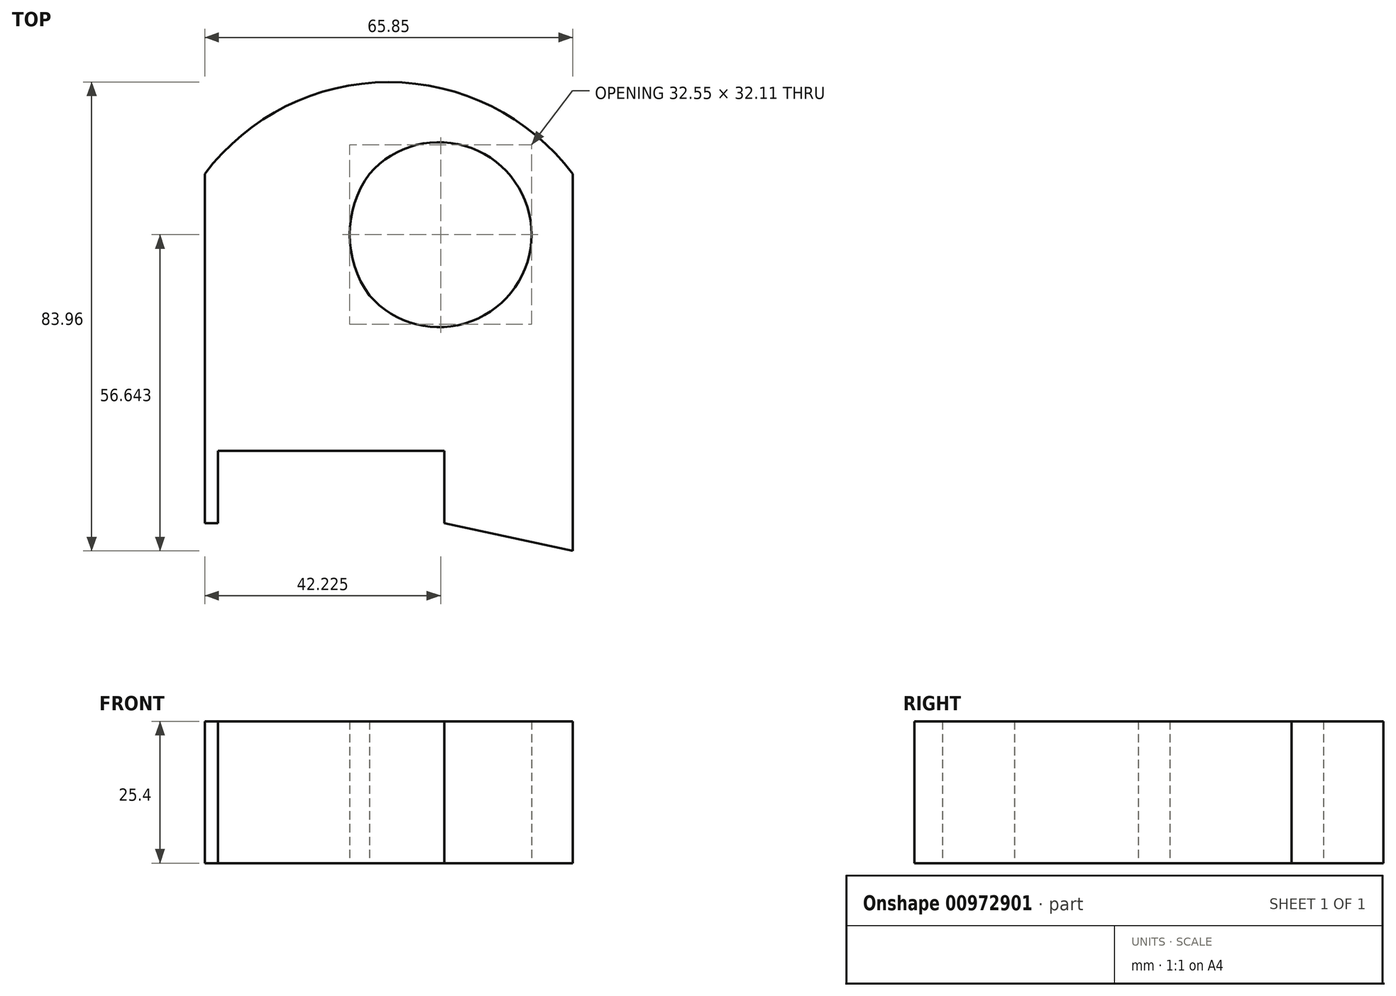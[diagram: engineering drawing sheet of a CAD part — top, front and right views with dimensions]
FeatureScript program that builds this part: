
annotation { "Feature Type Name" : "Feature", "Feature Type Description" : "" }
export const myFeature = defineFeature(function(context is Context, id is Id, definition is map)
    precondition{}
    {
        {
            var Q0;
            Q0=qCreatedBy(makeId("Top.planeOp"),FACE);
            var sketch = newSketch(context, id + "F0", { "sketchPlane" : qUnion([Q0])});
            skLineSegment(sketch, "E0", {"start": v(-29.46, -40.76) * mm, "end": v(-29.46, 21.77) * mm});
            skLineSegment(sketch, "E1", {"start": v(36.39, -45.76) * mm, "end": v(36.39, 21.77) * mm});
            skArc(sketch, "E2", {"start": v(36.39, 21.77) * mm, "mid": v(3.46, 38.2) * mm, "end": v(-29.46, 21.77) * mm});
            skArc(sketch, "E3", {"start": v(0, 0) * mm, "mid": v(29.04, 10.88) * mm, "end": v(0, 21.77) * mm});
            skArc(sketch, "E4", {"start": v(0, 21.77) * mm, "mid": v(-3.5, 10.88) * mm, "end": v(0, 0) * mm});
            skLineSegment(sketch, "E5", {"start": v(-29.46, -40.76) * mm, "end": v(-27.08, -40.76) * mm});
            skLineSegment(sketch, "E6", {"start": v(-27.08, -40.76) * mm, "end": v(-27.08, -27.85) * mm});
            skLineSegment(sketch, "E7", {"start": v(13.43, -27.85) * mm, "end": v(-27.08, -27.85) * mm});
            skLineSegment(sketch, "E8", {"start": v(13.43, -27.85) * mm, "end": v(13.43, -40.76) * mm});
            skLineSegment(sketch, "E9", {"start": v(13.43, -40.76) * mm, "end": v(36.39, -45.76) * mm});
            skSolve(sketch);
        }
        {
            var Q0;
            Q0 = qSketchRegion(id + "F0", true);
            extrude(context, id + "F1", {"entities" : qUnion([Q0]), "depth" : 25.4 * mm, "offsetDistance" : 25.4 * mm});
        }
    });
